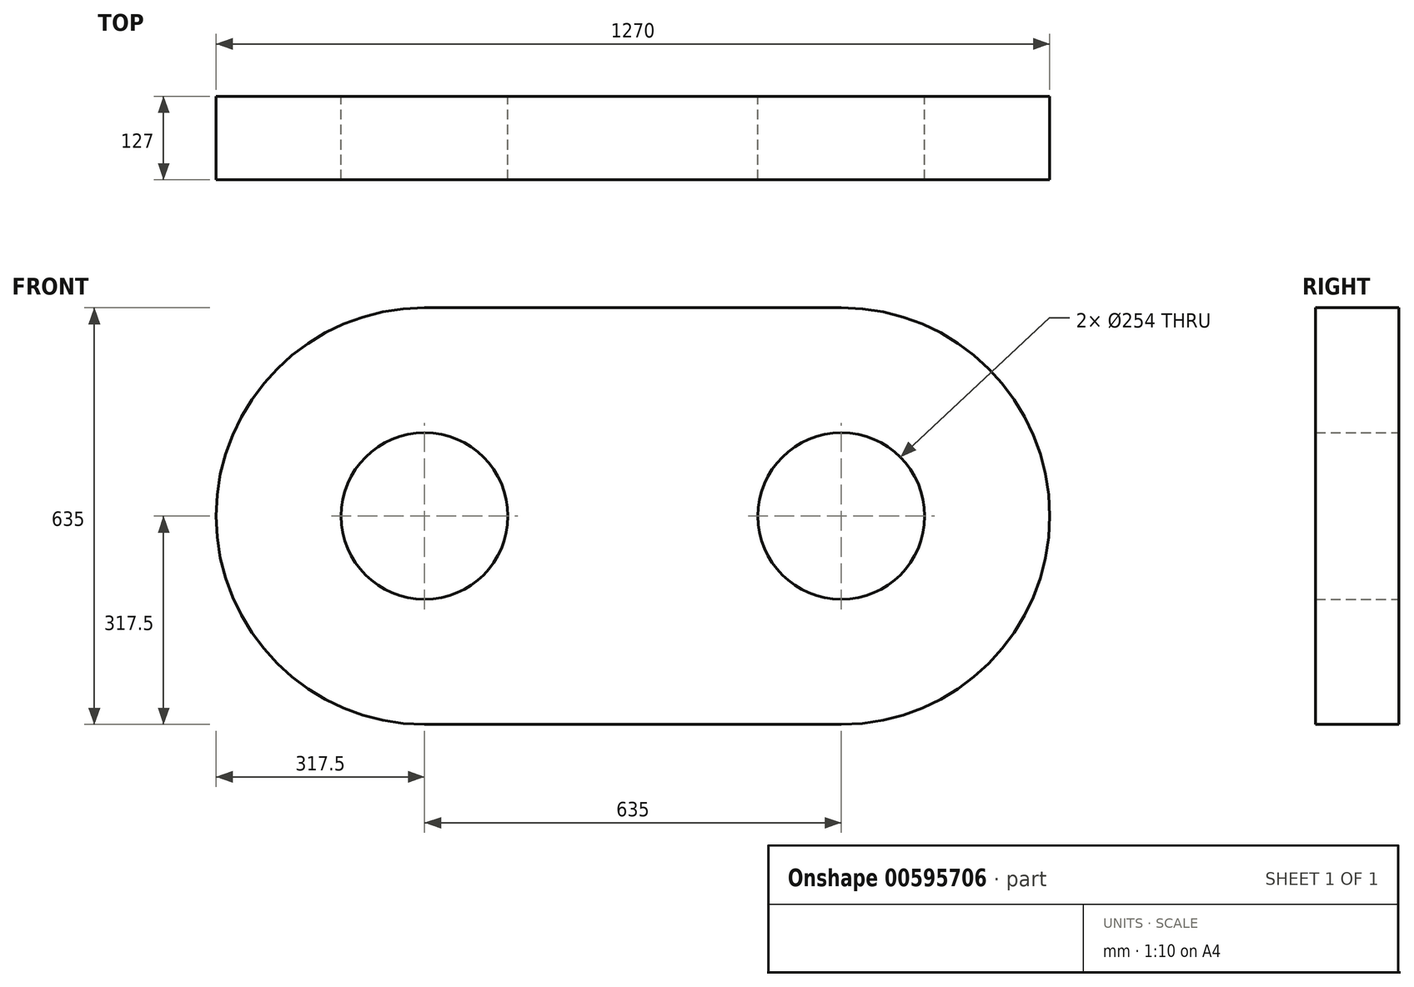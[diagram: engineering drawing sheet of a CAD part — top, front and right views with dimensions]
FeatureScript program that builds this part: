
annotation { "Feature Type Name" : "Feature", "Feature Type Description" : "" }
export const myFeature = defineFeature(function(context is Context, id is Id, definition is map)
    precondition{}
    {
        {
            var Q0;
            Q0=qCreatedBy(makeId("Front.planeOp"),FACE);
            var sketch = newSketch(context, id + "F0", { "sketchPlane" : qUnion([Q0])});
            skLineSegment(sketch, "E0.bottom", {"start": v(-317.5, 317.5) * mm, "end": v(317.5, 317.5) * mm});
            skLineSegment(sketch, "E0.top", {"start": v(-317.5, -317.5) * mm, "end": v(317.5, -317.5) * mm});
            skArc(sketch, "E1", {"start": v(-317.5, 317.5) * mm, "mid": v(-635, 0) * mm, "end": v(-317.5, -317.5) * mm});
            skArc(sketch, "E2", {"start": v(317.5, -317.5) * mm, "mid": v(635, 0) * mm, "end": v(317.5, 317.5) * mm});
            skCircle(sketch, "E3", {"center": v(317.5, 0) * mm, "radius": 127 * mm});
            skCircle(sketch, "E4", {"center": v(-317.5, 0) * mm, "radius": 127 * mm});
            skSolve(sketch);
        }
        {
            var Q0;
            Q0 = qSketchRegion(id + "F0", true);
            extrude(context, id + "F1", {"entities" : qUnion([Q0]), "endBound" : BoundingType.SYMMETRIC, "depth" : 127 * mm, "offsetDistance" : 25.4 * mm});
        }
    });
